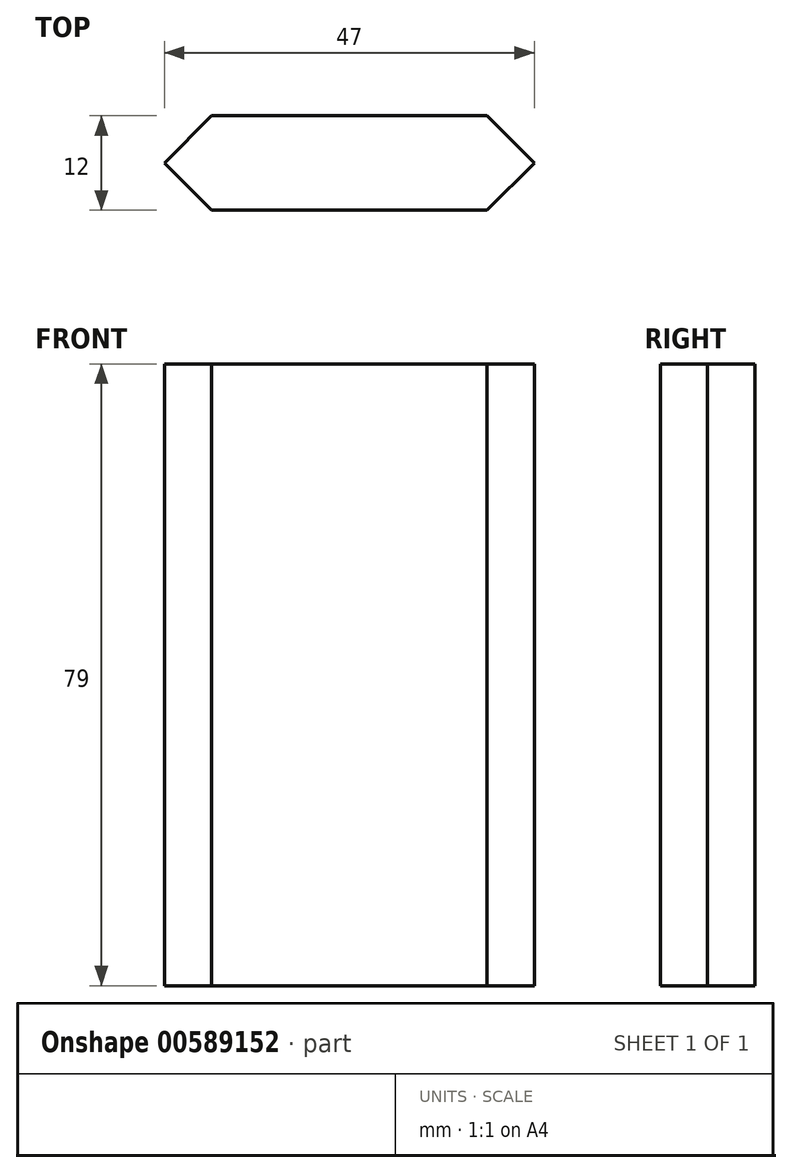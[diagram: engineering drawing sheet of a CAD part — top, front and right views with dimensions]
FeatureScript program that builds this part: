
annotation { "Feature Type Name" : "Feature", "Feature Type Description" : "" }
export const myFeature = defineFeature(function(context is Context, id is Id, definition is map)
    precondition{}
    {
        {
            var Q0;
            Q0=qCreatedBy(makeId("Top.planeOp"),FACE);
            var sketch = newSketch(context, id + "F0", { "sketchPlane" : qUnion([Q0])});
            skLineSegment(sketch, "E0.bottom", {"start": v(17.5, -6) * mm, "end": v(-17.5, -6) * mm, "construction": true});
            skLineSegment(sketch, "E0.top", {"start": v(17.5, 6) * mm, "end": v(-17.5, 6) * mm, "construction": true});
            skLineSegment(sketch, "E0.left", {"start": v(17.5, -6) * mm, "end": v(17.5, 6) * mm, "construction": true});
            skLineSegment(sketch, "E0.right", {"start": v(-17.5, -6) * mm, "end": v(-17.5, 6) * mm, "construction": true});
            skPoint(sketch, "E0.middle", {"position": v(0, 0) * mm});
            skLineSegment(sketch, "E1", {"start": v(-17.5, 6) * mm, "end": v(-23.5, 0) * mm, "construction": true});
            skPoint(sketch, "E1.endSnap0", {"position": v(-17.5, 0) * mm});
            skLineSegment(sketch, "E2", {"start": v(-23.5, 0) * mm, "end": v(-17.5, -6) * mm, "construction": true});
            skLineSegment(sketch, "E3", {"start": v(17.5, 6) * mm, "end": v(23.5, 0) * mm, "construction": true});
            skLineSegment(sketch, "E4", {"start": v(23.5, 0) * mm, "end": v(17.5, -6) * mm, "construction": true});
            skLineSegment(sketch, "E5", {"start": v(-23.5, 0) * mm, "end": v(-17.5, 6) * mm});
            skLineSegment(sketch, "E6", {"start": v(-17.5, 6) * mm, "end": v(17.5, 6) * mm});
            skLineSegment(sketch, "E7", {"start": v(17.5, 6) * mm, "end": v(23.5, 0) * mm});
            skLineSegment(sketch, "E8", {"start": v(23.5, 0) * mm, "end": v(17.5, -6) * mm});
            skLineSegment(sketch, "E9", {"start": v(17.5, -6) * mm, "end": v(-17.5, -6) * mm});
            skLineSegment(sketch, "E10", {"start": v(-17.5, -6) * mm, "end": v(-23.5, 0) * mm});
            skSolve(sketch);
        }
        {
            var Q0;
            Q0 = qSketchRegion(id + "F0", true);
            extrude(context, id + "F1", {"entities" : qUnion([Q0]), "depth" : 79 * mm, "offsetDistance" : 25.4 * mm});
        }
    });
